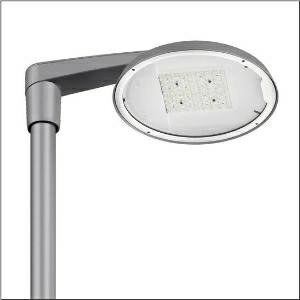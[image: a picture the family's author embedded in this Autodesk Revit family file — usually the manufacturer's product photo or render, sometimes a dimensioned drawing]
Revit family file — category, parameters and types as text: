
# Revit family: dl_50_iq_mini___st0_5a_5xa248b41f08ne_3c9a
name_source: partatom
category: Lighting Fixtures
units: mm (PartAtom-declared; Revit-internal decimal feet)

## family parameters
Cut with Voids When Loaded = No
Host = Face
Light Source = No
Part Type = Normal
Room Calculation Point = No
Round Connector Dimension = Use Diameter
Shared = No

## types (1)
- --- (1 x LED, 19390 lm, 115.8 W, 4000K)
    Apparent Load = 116 VA
    CIE Flux Codes = 43 76 97 100 100
    Color Rendering = 70
    Color Temperature = 4000K
    Default Elevation = 1800 mm
    Description = DL 50 iQ mini, mast luminaire, primary light control with lens, of PMMA, primary optical cover: cover, of toughened safety glass, transparent, light distribution: ST0.5a, light emission: direct distribution, primary light characteristic: asymmetric, installation type: side-entry, post-top, LED, High Power LED, rated luminous flux: 19.390lm, luminous efficacy: 167lm/W, light colour: 740, colour temperature: 4000K, control gear: iQ Street-Remote, control: optimised constant luminous flux control (CLO 2.0), Desk-Remote (wireless, voltage-free reading and setting of iQ features in the workshop via application-optimized NFC function/RFID function), Light-Fading, Smart-Wire, Night-Set, Lumen-Switch, Temp-Guard, Auto-Match, Street-Remote, mains connection: 230..240V, AC, 50/60Hz, connection cable pre-assembled, cable length: 10,5m, start of lifetime: 116W, end of service life: 127W, reduction: 53W, luminaire housing, of diecast aluminium, powder-coated, SITECO metallic grey (DB 702S), inclination adjustable: 0°, 5°, 10° (post-top) | 0°, -5°, -10°, -15° (side-entry), please order mast post-top element or mast side-entry element separately, diameter: 500mm, height: 115mm, post-top: for spigot size d x l = 76 x 100mm; with reducer (optional accessory) 60 x 100mm | side-entry: for spigot size d x l = 60 x 100mm; with reducer (optional accessory) 42 x 100mm, mounting height: 4..6m, protection rating (complete): IP66, insulation class (complete): insulation class II (safety insulation), certification: CE, ENEC, ENEC+, VDE, impact resistance: IK08, permissible operating ambient temperature for outdoor applications: -25..+40°C, standard-compliant lighting for roads and squares, packaging unit: 1 piece

Light Distribution: ST0.5a
    Height = 115 mm
    Lamp = 1 x LED
    Lamp Light Flux = 19390 lm
    Lamp Power = 115.8 W
    Lamp count = 1
    Length = 500 mm
    Luminous efficacy = 167 lm/W
    Manufacturer = Siteco
    ModVariant = No
    Model = 5XA248B41F08NE
    Number of Poles = 1
    OnlyDefault = Yes
    Power Factor = 1
    Product Name = DL 50 iQ mini | ST0.5a
    Product group = mast luminaire | pylon top
    ProductGroupID = 6100
    Protection Class = Protection class II
    Protection Degree = IP 66
    RLX_Detail_Level = 1
    RLX_Emergency_Light_Flux = 0 lm
    RLX_Emergency_Type = 0
    RLX_Emergency_Type_DB = No
    RlxData = <blob elided: 128349 chars, md5=65549e54>
    Socket = socket
    Standby Power = 0 W
    System Light Flux = 19390 lm
    System Power = 116 W
    Type Comments = factory setting: luminous flux: 100 % | dim-lin: 254 | 626 mA
    Type Image = l_1251790.jpg
    URL = http://relux.com
    VarID = @adj_142301
    Voltage = 0 V
    Weight = 0.00 kg
    Width = 0 mm  [stored 0 ft]

note: [stored X ft] marks values corroborated as IEEE doubles in the binary element streams (Revit-internal decimal feet)

## geometry (parser evidence)
native form markers: Blend x4, Sweep x9
no freeform markers — native parametric forms only
